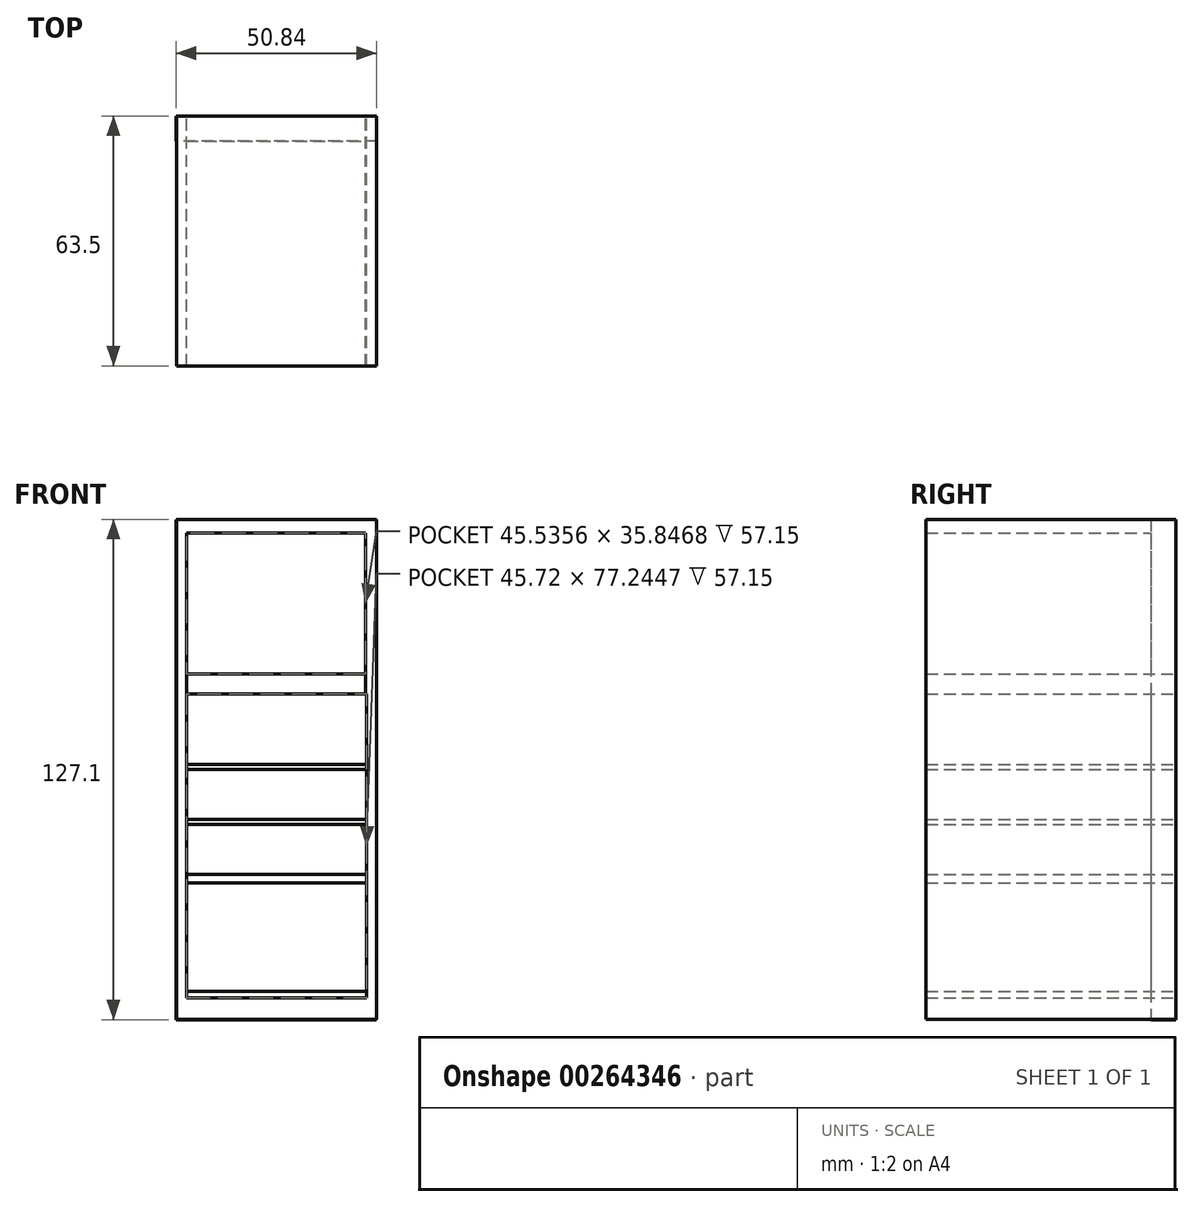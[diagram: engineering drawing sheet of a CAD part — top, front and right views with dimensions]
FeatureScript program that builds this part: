
annotation { "Feature Type Name" : "Feature", "Feature Type Description" : "" }
export const myFeature = defineFeature(function(context is Context, id is Id, definition is map)
    precondition{}
    {
        {
            var Q0;
            Q0=qCreatedBy(makeId("Front.planeOp"),FACE);
            var sketch = newSketch(context, id + "F0", { "sketchPlane" : qUnion([Q0])});
            skLineSegment(sketch, "E0.bottom", {"start": v(25.4, 63.5) * mm, "end": v(-25.4, 63.5) * mm});
            skLineSegment(sketch, "E0.top", {"start": v(25.4, -63.5) * mm, "end": v(-25.4, -63.5) * mm});
            skLineSegment(sketch, "E0.left", {"start": v(25.4, 63.5) * mm, "end": v(25.4, -63.5) * mm});
            skLineSegment(sketch, "E0.right", {"start": v(-25.4, 63.5) * mm, "end": v(-25.4, -63.5) * mm});
            skPoint(sketch, "E0.middle", {"position": v(0, 0) * mm});
            skLineSegment(sketch, "E1", {"start": v(-25.4, 51.07) * mm, "end": v(-22.86, 51.07) * mm});
            skLineSegment(sketch, "E2", {"start": v(-22.86, 63.5) * mm, "end": v(-22.86, 60.1) * mm});
            skLineSegment(sketch, "E3", {"start": v(25.4, 51.07) * mm, "end": v(22.86, 51.07) * mm});
            skLineSegment(sketch, "E4", {"start": v(22.86, 63.5) * mm, "end": v(22.86, 60.96) * mm});
            skLineSegment(sketch, "E5.bottom", {"start": v(-22.86, 60.1) * mm, "end": v(22.68, 60.1) * mm});
            skLineSegment(sketch, "E5.top", {"start": v(-22.86, 24.25) * mm, "end": v(22.68, 24.25) * mm});
            skLineSegment(sketch, "E5.left", {"start": v(-22.86, 60.1) * mm, "end": v(-22.86, 24.25) * mm});
            skLineSegment(sketch, "E5.right", {"start": v(22.68, 60.1) * mm, "end": v(22.68, 24.25) * mm});
            skLineSegment(sketch, "E6", {"start": v(-22.86, 24.25) * mm, "end": v(-22.86, 19.17) * mm});
            skLineSegment(sketch, "E7", {"start": v(22.68, 24.25) * mm, "end": v(22.68, 19.17) * mm});
            skLineSegment(sketch, "E8", {"start": v(0, -63.5) * mm, "end": v(0, -58.62) * mm});
            skPoint(sketch, "E8.endSnap0", {"position": v(0, -63.5) * mm});
            skLineSegment(sketch, "E9.bottom", {"start": v(-22.86, 19.17) * mm, "end": v(22.86, 19.17) * mm});
            skLineSegment(sketch, "E9.top", {"start": v(-22.86, -58.07) * mm, "end": v(22.86, -58.07) * mm});
            skLineSegment(sketch, "E9.left", {"start": v(-22.86, 19.17) * mm, "end": v(-22.86, -58.07) * mm});
            skLineSegment(sketch, "E9.right", {"start": v(22.86, 19.17) * mm, "end": v(22.86, -58.07) * mm});
            skLineSegment(sketch, "E10.bottom", {"start": v(-22.86, 0) * mm, "end": v(22.86, 0) * mm});
            skLineSegment(sketch, "E10.top", {"start": v(-22.86, -12.7) * mm, "end": v(22.86, -12.7) * mm});
            skLineSegment(sketch, "E10.left", {"start": v(-22.86, 0) * mm, "end": v(-22.86, -12.7) * mm});
            skLineSegment(sketch, "E10.right", {"start": v(22.86, 0) * mm, "end": v(22.86, -12.7) * mm});
            skLineSegment(sketch, "E11.top", {"start": v(-22.86, -13.97) * mm, "end": v(22.86, -13.97) * mm});
            skLineSegment(sketch, "E11.left", {"start": v(-22.86, -12.7) * mm, "end": v(-22.86, -13.97) * mm});
            skLineSegment(sketch, "E11.right", {"start": v(22.86, -12.7) * mm, "end": v(22.86, -13.97) * mm});
            skLineSegment(sketch, "E12.left", {"start": v(-22.86, 2.77) * mm, "end": v(-22.86, 0) * mm});
            skLineSegment(sketch, "E12.right", {"start": v(22.86, 2.77) * mm, "end": v(22.86, 0) * mm});
            skLineSegment(sketch, "E13.top", {"start": v(-22.86, 1.27) * mm, "end": v(22.86, 1.27) * mm});
            skLineSegment(sketch, "E13.left", {"start": v(-22.86, 0) * mm, "end": v(-22.86, 1.27) * mm});
            skLineSegment(sketch, "E13.right", {"start": v(22.86, 0) * mm, "end": v(22.86, 1.27) * mm});
            skLineSegment(sketch, "E14.left", {"start": v(-22.86, -13.97) * mm, "end": v(-22.86, -28.82) * mm});
            skLineSegment(sketch, "E14.right", {"start": v(22.86, -13.97) * mm, "end": v(22.86, -28.82) * mm});
            skLineSegment(sketch, "E15.top", {"start": v(-22.86, -26.67) * mm, "end": v(22.86, -26.67) * mm});
            skLineSegment(sketch, "E15.left", {"start": v(-22.86, -13.97) * mm, "end": v(-22.86, -26.67) * mm});
            skLineSegment(sketch, "E15.right", {"start": v(22.86, -13.97) * mm, "end": v(22.86, -26.67) * mm});
            skLineSegment(sketch, "E16.left", {"start": v(-22.86, -26.67) * mm, "end": v(-22.86, -30.97) * mm});
            skLineSegment(sketch, "E16.right", {"start": v(22.86, -26.67) * mm, "end": v(22.86, -30.97) * mm});
            skLineSegment(sketch, "E17.left", {"start": v(-22.86, -26.67) * mm, "end": v(-22.86, -28.82) * mm});
            skLineSegment(sketch, "E17.right", {"start": v(22.86, -26.67) * mm, "end": v(22.86, -28.82) * mm});
            skLineSegment(sketch, "E18.bottom", {"start": v(-22.86, -28.82) * mm, "end": v(22.86, -28.82) * mm});
            skLineSegment(sketch, "E18.left", {"start": v(-22.86, -28.82) * mm, "end": v(-22.86, -26.67) * mm});
            skLineSegment(sketch, "E18.right", {"start": v(22.86, -28.82) * mm, "end": v(22.86, -26.67) * mm});
            skLineSegment(sketch, "E19.bottom", {"start": v(-22.86, -30.97) * mm, "end": v(22.86, -30.97) * mm});
            skLineSegment(sketch, "E19.top", {"start": v(-22.86, -56.37) * mm, "end": v(22.86, -56.37) * mm});
            skLineSegment(sketch, "E19.left", {"start": v(-22.86, -30.97) * mm, "end": v(-22.86, -56.37) * mm});
            skLineSegment(sketch, "E19.right", {"start": v(22.86, -30.97) * mm, "end": v(22.86, -56.37) * mm});
            skSolve(sketch);
        }
        {
            var Q0;
            {var subQ0=sQuery(id+"F0.wireOp",EDGE,"E1");Q0=makeQuery(id+"F0.imprint","IMPRINT",FACE,{"disambiguationData":[TD([[makeQuery(id+"F0.imprint","IMPRINT",EDGE,{"derivedFrom":subQ0}),-1.0]])]});}
            var Q1;
            Q1=makeQuery(id+"F0.imprint","IMPRINT",FACE,{"disambiguationData":[TD([[makeQuery(id+"F0.imprint","IMPRINT",EDGE,{"derivedFrom":sQuery(id+"F0.wireOp",EDGE,"E5.top")}),-1.0]])]});
            var Q2;
            {var subQ1=sQuery(id+"F0.wireOp",EDGE,"E1");Q2=makeQuery(id+"F0.imprint","IMPRINT",FACE,{"disambiguationData":[TD([[makeQuery(id+"F0.imprint","IMPRINT",EDGE,{"derivedFrom":subQ1}),1.0]])]});}
            extrude(context, id + "F1", {"entities" : qUnion([Q0, Q1, Q2]), "depth" : 63.5 * mm});
        }
        {
            var Q0;
            Q0=qCreatedBy(makeId("Front.planeOp"),FACE);
            var sketch = newSketch(context, id + "F2", { "sketchPlane" : qUnion([Q0])});
            skLineSegment(sketch, "E20.bottom", {"start": v(25.36, 63.4) * mm, "end": v(-25.44, 63.4) * mm});
            skLineSegment(sketch, "E20.top", {"start": v(25.36, -63.6) * mm, "end": v(-25.44, -63.6) * mm});
            skLineSegment(sketch, "E20.left", {"start": v(25.36, 63.4) * mm, "end": v(25.36, -63.6) * mm});
            skLineSegment(sketch, "E20.right", {"start": v(-25.44, 63.4) * mm, "end": v(-25.44, -63.6) * mm});
            skSolve(sketch);
        }
        {
            var Q0;
            Q0=makeQuery(id+"F2.imprint","IMPRINT",FACE,{"disambiguationData":[TD([[makeQuery(id+"F2.imprint","IMPRINT",EDGE,{"derivedFrom":sQuery(id+"F2.wireOp",EDGE,"E20.bottom")}),1.0]])]});
            extrude(context, id + "F3", {"entities" : qUnion([Q0]), "operationType" : NewBodyOperationType.ADD, "depth" : 6.35 * mm});
        }
        {
            var Q0;
            Q0=makeQuery(id+"F0.imprint","IMPRINT",FACE,{"disambiguationData":[TD([[makeQuery(id+"F0.imprint","IMPRINT",EDGE,{"derivedFrom":sQuery(id+"F0.wireOp",EDGE,"E10.bottom")}),1.0]])]});
            var Q1;
            Q1=makeQuery(id+"F0.imprint","IMPRINT",FACE,{"disambiguationData":[TD([[makeQuery(id+"F0.imprint","IMPRINT",EDGE,{"derivedFrom":sQuery(id+"F0.wireOp",EDGE,"E10.top")}),-1.0]])]});
            var Q2;
            Q2=makeQuery(id+"F0.imprint","IMPRINT",FACE,{"disambiguationData":[TD([[makeQuery(id+"F0.imprint","IMPRINT",EDGE,{"derivedFrom":sQuery(id+"F0.wireOp",EDGE,"E18.bottom")}),1.0]])]});
            var Q3;
            Q3=makeQuery(id+"F0.imprint","IMPRINT",FACE,{"disambiguationData":[TD([[makeQuery(id+"F0.imprint","IMPRINT",EDGE,{"derivedFrom":sQuery(id+"F0.wireOp",EDGE,"E5.top")}),-1.0]])]});
            var Q4;
            {var subQ0=sQuery(id+"F0.wireOp",EDGE,"E9.top");Q4=makeQuery(id+"F0.imprint","IMPRINT",FACE,{"disambiguationData":[TD([[makeQuery(id+"F0.imprint","IMPRINT",EDGE,{"derivedFrom":subQ0}),1.0]])]});}
            extrude(context, id + "F4", {"entities" : qUnion([Q0, Q1, Q2, Q3, Q4]), "depth" : 63.5 * mm});
        }
    });
